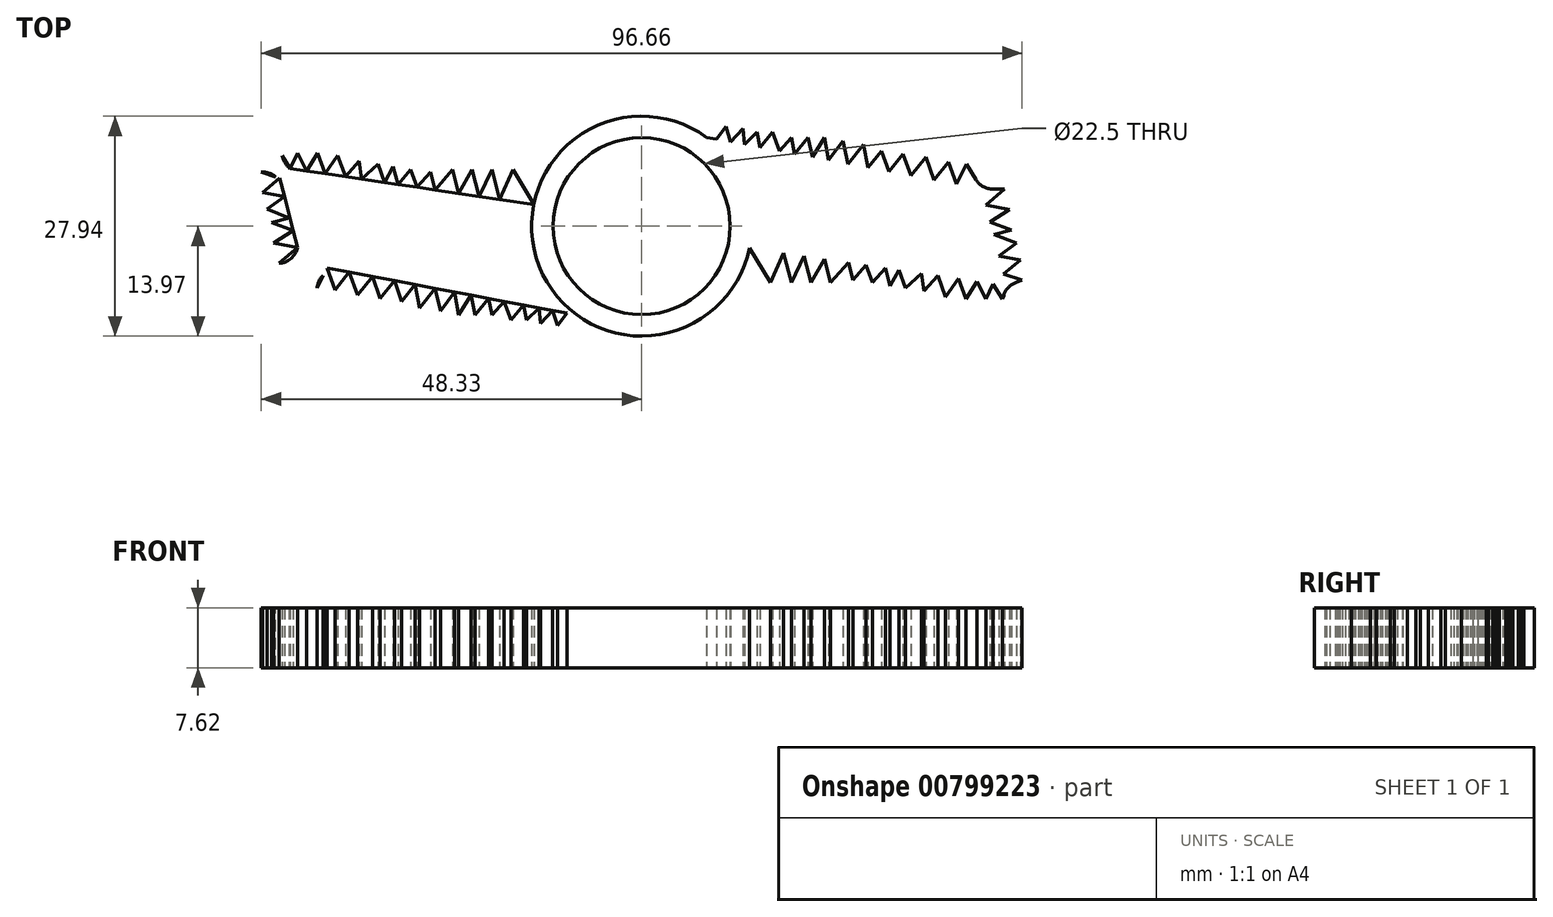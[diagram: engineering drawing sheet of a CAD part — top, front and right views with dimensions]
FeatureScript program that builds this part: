
annotation { "Feature Type Name" : "Feature", "Feature Type Description" : "" }
export const myFeature = defineFeature(function(context is Context, id is Id, definition is map)
    precondition{}
    {
        {
            var Q0;
            Q0=qCreatedBy(makeId("Top.planeOp"),FACE);
            var sketch = newSketch(context, id + "F0", { "sketchPlane" : qUnion([Q0])});
            skCircle(sketch, "E0", {"center": v(0, 0) * mm, "radius": 11.25 * mm});
            skCircle(sketch, "E1", {"center": v(0, 0) * mm, "radius": 13.97 * mm});
            skLineSegment(sketch, "E2", {"start": v(8.24, 11.28) * mm, "end": v(43.2, 4.72) * mm});
            skLineSegment(sketch, "E3", {"start": v(43.2, 4.72) * mm, "end": v(46.36, -7.58) * mm});
            skLineSegment(sketch, "E4", {"start": v(46.36, -7.58) * mm, "end": v(13.7, -2.76) * mm});
            skLineSegment(sketch, "E5.1.0", {"start": v(-43.2, -4.72) * mm, "end": v(-46.36, 7.58) * mm});
            skLineSegment(sketch, "E5.1.1", {"start": v(-8.24, -11.28) * mm, "end": v(-43.2, -4.72) * mm});
            skLineSegment(sketch, "E5.1.2", {"start": v(-46.36, 7.58) * mm, "end": v(-13.7, 2.76) * mm});
            skLineSegment(sketch, "E6", {"start": v(9.5, 11.04) * mm, "end": v(10.7, 12.64) * mm});
            skLineSegment(sketch, "E7", {"start": v(10.7, 12.64) * mm, "end": v(11.3, 10.7) * mm});
            skLineSegment(sketch, "E8", {"start": v(11.3, 10.7) * mm, "end": v(12.87, 12.4) * mm});
            skLineSegment(sketch, "E9", {"start": v(12.87, 12.4) * mm, "end": v(13.06, 10.37) * mm});
            skLineSegment(sketch, "E10", {"start": v(13.06, 10.37) * mm, "end": v(14.64, 11.95) * mm});
            skLineSegment(sketch, "E11", {"start": v(14.64, 11.95) * mm, "end": v(15.02, 10) * mm});
            skLineSegment(sketch, "E12", {"start": v(15.02, 10) * mm, "end": v(16.61, 11.95) * mm});
            skLineSegment(sketch, "E13", {"start": v(16.61, 11.95) * mm, "end": v(17.49, 9.54) * mm});
            skLineSegment(sketch, "E14", {"start": v(17.49, 9.54) * mm, "end": v(19.02, 11.28) * mm});
            skLineSegment(sketch, "E15", {"start": v(19.02, 11.28) * mm, "end": v(19.44, 9.18) * mm});
            skLineSegment(sketch, "E16", {"start": v(19.44, 9.18) * mm, "end": v(21.14, 11.28) * mm});
            skLineSegment(sketch, "E17", {"start": v(21.14, 11.28) * mm, "end": v(21.7, 8.75) * mm});
            skLineSegment(sketch, "E18", {"start": v(21.7, 8.75) * mm, "end": v(23.24, 11.28) * mm});
            skLineSegment(sketch, "E19", {"start": v(23.24, 11.28) * mm, "end": v(23.75, 8.37) * mm});
            skLineSegment(sketch, "E20", {"start": v(23.75, 8.37) * mm, "end": v(25.57, 10.79) * mm});
            skLineSegment(sketch, "E21", {"start": v(25.57, 10.79) * mm, "end": v(26.21, 7.9) * mm});
            skLineSegment(sketch, "E22", {"start": v(26.21, 7.9) * mm, "end": v(28.2, 10.37) * mm});
            skLineSegment(sketch, "E23", {"start": v(28.2, 10.37) * mm, "end": v(28.77, 7.42) * mm});
            skLineSegment(sketch, "E24", {"start": v(28.77, 7.42) * mm, "end": v(30.48, 9.54) * mm});
            skLineSegment(sketch, "E25", {"start": v(30.48, 9.54) * mm, "end": v(31.41, 6.93) * mm});
            skLineSegment(sketch, "E26", {"start": v(31.41, 6.93) * mm, "end": v(33.22, 9.18) * mm});
            skLineSegment(sketch, "E27", {"start": v(33.22, 9.18) * mm, "end": v(34.2, 6.4) * mm});
            skLineSegment(sketch, "E28", {"start": v(34.2, 6.4) * mm, "end": v(36.1, 8.75) * mm});
            skLineSegment(sketch, "E29", {"start": v(36.1, 8.75) * mm, "end": v(37.13, 5.85) * mm});
            skLineSegment(sketch, "E30", {"start": v(37.13, 5.85) * mm, "end": v(38.97, 8.14) * mm});
            skLineSegment(sketch, "E31", {"start": v(38.97, 8.14) * mm, "end": v(39.97, 5.32) * mm});
            skLineSegment(sketch, "E32", {"start": v(39.97, 5.32) * mm, "end": v(41.25, 7.88) * mm});
            skLineSegment(sketch, "E33", {"start": v(41.25, 7.88) * mm, "end": v(43.2, 4.72) * mm});
            skLineSegment(sketch, "E34", {"start": v(43.2, 4.72) * mm, "end": v(46.07, 4.72) * mm});
            skLineSegment(sketch, "E35", {"start": v(46.07, 4.72) * mm, "end": v(43.71, 2.7) * mm});
            skLineSegment(sketch, "E36", {"start": v(43.71, 2.7) * mm, "end": v(46.74, 2.14) * mm});
            skLineSegment(sketch, "E37", {"start": v(46.74, 2.14) * mm, "end": v(44.27, 0.54) * mm});
            skLineSegment(sketch, "E38", {"start": v(44.27, 0.54) * mm, "end": v(47, -0.48) * mm});
            skLineSegment(sketch, "E39", {"start": v(47, -0.48) * mm, "end": v(44.78, -1.06) * mm});
            skPoint(sketch, "E39.endSnap0", {"position": v(44.78, -1.43) * mm});
            skLineSegment(sketch, "E40", {"start": v(44.78, -1.06) * mm, "end": v(47.6, -2.15) * mm});
            skLineSegment(sketch, "E41", {"start": v(47.6, -2.15) * mm, "end": v(45.38, -3.78) * mm});
            skLineSegment(sketch, "E42", {"start": v(45.38, -3.78) * mm, "end": v(48.14, -4.3) * mm});
            skLineSegment(sketch, "E43", {"start": v(48.14, -4.3) * mm, "end": v(45.98, -6.1) * mm});
            skLineSegment(sketch, "E44", {"start": v(45.98, -6.1) * mm, "end": v(48.33, -6.86) * mm});
            skLineSegment(sketch, "E45", {"start": v(48.33, -6.86) * mm, "end": v(46.36, -7.58) * mm});
            skLineSegment(sketch, "E46", {"start": v(46.36, -7.58) * mm, "end": v(45.84, -9.27) * mm});
            skLineSegment(sketch, "E47", {"start": v(45.84, -9.27) * mm, "end": v(44.64, -7.33) * mm});
            skLineSegment(sketch, "E48", {"start": v(44.64, -7.33) * mm, "end": v(43.72, -9.27) * mm});
            skLineSegment(sketch, "E49", {"start": v(43.72, -9.27) * mm, "end": v(42.59, -7.02) * mm});
            skLineSegment(sketch, "E50", {"start": v(42.59, -7.02) * mm, "end": v(41.18, -9.27) * mm});
            skLineSegment(sketch, "E51", {"start": v(41.18, -9.27) * mm, "end": v(40.23, -6.68) * mm});
            skLineSegment(sketch, "E52", {"start": v(40.23, -6.68) * mm, "end": v(38.6, -8.98) * mm});
            skLineSegment(sketch, "E53", {"start": v(38.6, -8.98) * mm, "end": v(37.62, -6.3) * mm});
            skLineSegment(sketch, "E54", {"start": v(37.62, -6.3) * mm, "end": v(35.88, -8.25) * mm});
            skLineSegment(sketch, "E55", {"start": v(35.88, -8.25) * mm, "end": v(35.56, -5.99) * mm});
            skLineSegment(sketch, "E56", {"start": v(35.56, -5.99) * mm, "end": v(33.5, -7.89) * mm});
            skLineSegment(sketch, "E57", {"start": v(33.5, -7.89) * mm, "end": v(32.66, -5.56) * mm});
            skLineSegment(sketch, "E58", {"start": v(32.66, -5.56) * mm, "end": v(31.55, -7.58) * mm});
            skLineSegment(sketch, "E59", {"start": v(31.55, -7.58) * mm, "end": v(30.97, -5.3) * mm});
            skLineSegment(sketch, "E60", {"start": v(30.97, -5.3) * mm, "end": v(29.33, -7.16) * mm});
            skLineSegment(sketch, "E61", {"start": v(29.33, -7.16) * mm, "end": v(28.52, -4.95) * mm});
            skLineSegment(sketch, "E62", {"start": v(28.52, -4.95) * mm, "end": v(26.84, -6.86) * mm});
            skLineSegment(sketch, "E63", {"start": v(26.84, -6.86) * mm, "end": v(26.26, -4.61) * mm});
            skLineSegment(sketch, "E64", {"start": v(26.26, -4.61) * mm, "end": v(24, -7.16) * mm});
            skLineSegment(sketch, "E65", {"start": v(24, -7.16) * mm, "end": v(23.23, -4.17) * mm});
            skLineSegment(sketch, "E66", {"start": v(23.23, -4.17) * mm, "end": v(21.52, -7.16) * mm});
            skLineSegment(sketch, "E67", {"start": v(21.52, -7.16) * mm, "end": v(20.65, -3.78) * mm});
            skLineSegment(sketch, "E68", {"start": v(20.65, -3.78) * mm, "end": v(19.02, -7.16) * mm});
            skLineSegment(sketch, "E69", {"start": v(19.02, -7.16) * mm, "end": v(18.05, -3.4) * mm});
            skLineSegment(sketch, "E70", {"start": v(18.05, -3.4) * mm, "end": v(16.35, -7.16) * mm});
            skLineSegment(sketch, "E71", {"start": v(16.35, -7.16) * mm, "end": v(13.7, -2.76) * mm});
            skPoint(sketch, "E72.1.0", {"position": v(-44.78, 1.43) * mm});
            skLineSegment(sketch, "E72.1.1", {"start": v(-41.18, 9.27) * mm, "end": v(-40.23, 6.68) * mm});
            skLineSegment(sketch, "E72.1.2", {"start": v(-38.6, 8.98) * mm, "end": v(-37.62, 6.3) * mm});
            skLineSegment(sketch, "E72.1.3", {"start": v(-39.97, -5.32) * mm, "end": v(-41.25, -7.88) * mm});
            skLineSegment(sketch, "E72.1.4", {"start": v(-35.88, 8.25) * mm, "end": v(-35.56, 5.99) * mm});
            skLineSegment(sketch, "E72.1.5", {"start": v(-28.2, -10.37) * mm, "end": v(-28.77, -7.42) * mm});
            skLineSegment(sketch, "E72.1.6", {"start": v(-43.71, -2.7) * mm, "end": v(-46.74, -2.14) * mm});
            skLineSegment(sketch, "E72.1.7", {"start": v(-30.48, -9.54) * mm, "end": v(-31.41, -6.93) * mm});
            skLineSegment(sketch, "E72.1.9", {"start": v(-44.64, 7.33) * mm, "end": v(-43.72, 9.27) * mm});
            skLineSegment(sketch, "E72.1.10", {"start": v(-34.2, -6.4) * mm, "end": v(-36.1, -8.75) * mm});
            skLineSegment(sketch, "E72.1.11", {"start": v(-19.44, -9.18) * mm, "end": v(-21.14, -11.28) * mm});
            skLineSegment(sketch, "E72.1.12", {"start": v(-10.7, -12.64) * mm, "end": v(-11.3, -10.7) * mm});
            skLineSegment(sketch, "E72.1.13", {"start": v(-16.35, 7.16) * mm, "end": v(-13.7, 2.76) * mm});
            skLineSegment(sketch, "E72.1.14", {"start": v(-28.77, -7.42) * mm, "end": v(-30.48, -9.54) * mm});
            skLineSegment(sketch, "E72.1.15", {"start": v(-16.61, -11.95) * mm, "end": v(-17.49, -9.54) * mm});
            skLineSegment(sketch, "E72.1.16", {"start": v(-13.06, -10.37) * mm, "end": v(-14.64, -11.95) * mm});
            skLineSegment(sketch, "E72.1.17", {"start": v(-23.75, -8.37) * mm, "end": v(-25.57, -10.79) * mm});
            skLineSegment(sketch, "E72.1.18", {"start": v(-31.41, -6.93) * mm, "end": v(-33.22, -9.18) * mm});
            skLineSegment(sketch, "E72.1.19", {"start": v(-33.22, -9.18) * mm, "end": v(-34.2, -6.4) * mm});
            skLineSegment(sketch, "E72.1.20", {"start": v(-23.24, -11.28) * mm, "end": v(-23.75, -8.37) * mm});
            skLineSegment(sketch, "E72.1.21", {"start": v(-23.23, 4.17) * mm, "end": v(-21.52, 7.16) * mm});
            skLineSegment(sketch, "E72.1.22", {"start": v(-19.02, -11.28) * mm, "end": v(-19.44, -9.18) * mm});
            skLineSegment(sketch, "E72.1.23", {"start": v(-25.57, -10.79) * mm, "end": v(-26.21, -7.9) * mm});
            skLineSegment(sketch, "E72.1.24", {"start": v(-46.74, -2.14) * mm, "end": v(-44.27, -0.54) * mm});
            skLineSegment(sketch, "E72.1.25", {"start": v(-26.84, 6.86) * mm, "end": v(-26.26, 4.61) * mm});
            skLineSegment(sketch, "E72.1.26", {"start": v(-43.72, 9.27) * mm, "end": v(-42.59, 7.02) * mm});
            skLineSegment(sketch, "E72.1.27", {"start": v(-38.97, -8.14) * mm, "end": v(-39.97, -5.32) * mm});
            skLineSegment(sketch, "E72.1.28", {"start": v(-40.23, 6.68) * mm, "end": v(-38.6, 8.98) * mm});
            skLineSegment(sketch, "E72.1.29", {"start": v(-21.14, -11.28) * mm, "end": v(-21.7, -8.75) * mm});
            skLineSegment(sketch, "E72.1.30", {"start": v(-21.7, -8.75) * mm, "end": v(-23.24, -11.28) * mm});
            skLineSegment(sketch, "E72.1.31", {"start": v(-35.56, 5.99) * mm, "end": v(-33.5, 7.89) * mm});
            skLineSegment(sketch, "E72.1.32", {"start": v(-26.26, 4.61) * mm, "end": v(-24, 7.16) * mm});
            skLineSegment(sketch, "E72.1.33", {"start": v(-24, 7.16) * mm, "end": v(-23.23, 4.17) * mm});
            skLineSegment(sketch, "E72.1.34", {"start": v(-15.02, -10) * mm, "end": v(-16.61, -11.95) * mm});
            skLineSegment(sketch, "E72.1.35", {"start": v(-36.1, -8.75) * mm, "end": v(-37.13, -5.85) * mm});
            skLineSegment(sketch, "E72.1.36", {"start": v(-42.59, 7.02) * mm, "end": v(-41.18, 9.27) * mm});
            skLineSegment(sketch, "E72.1.38", {"start": v(-21.52, 7.16) * mm, "end": v(-20.65, 3.78) * mm});
            skLineSegment(sketch, "E72.1.39", {"start": v(-11.3, -10.7) * mm, "end": v(-12.87, -12.4) * mm});
            skLineSegment(sketch, "E72.1.40", {"start": v(-37.62, 6.3) * mm, "end": v(-35.88, 8.25) * mm});
            skLineSegment(sketch, "E72.1.41", {"start": v(-37.13, -5.85) * mm, "end": v(-38.97, -8.14) * mm});
            skLineSegment(sketch, "E72.1.42", {"start": v(-26.21, -7.9) * mm, "end": v(-28.2, -10.37) * mm});
            skLineSegment(sketch, "E72.1.43", {"start": v(-28.52, 4.95) * mm, "end": v(-26.84, 6.86) * mm});
            skLineSegment(sketch, "E72.1.44", {"start": v(-12.87, -12.4) * mm, "end": v(-13.06, -10.37) * mm});
            skLineSegment(sketch, "E72.1.45", {"start": v(-29.33, 7.16) * mm, "end": v(-28.52, 4.95) * mm});
            skLineSegment(sketch, "E72.1.46", {"start": v(-41.25, -7.88) * mm, "end": v(-43.2, -4.72) * mm});
            skLineSegment(sketch, "E72.1.47", {"start": v(-46.07, -4.72) * mm, "end": v(-43.71, -2.7) * mm});
            skLineSegment(sketch, "E72.1.48", {"start": v(-20.65, 3.78) * mm, "end": v(-19.02, 7.16) * mm});
            skLineSegment(sketch, "E72.1.49", {"start": v(-9.5, -11.04) * mm, "end": v(-10.7, -12.64) * mm});
            skLineSegment(sketch, "E72.1.50", {"start": v(-44.78, 1.06) * mm, "end": v(-47.6, 2.15) * mm});
            skLineSegment(sketch, "E72.1.51", {"start": v(-14.64, -11.95) * mm, "end": v(-15.02, -10) * mm});
            skLineSegment(sketch, "E72.1.52", {"start": v(-43.2, -4.72) * mm, "end": v(-46.07, -4.72) * mm});
            skLineSegment(sketch, "E72.1.53", {"start": v(-18.05, 3.4) * mm, "end": v(-16.35, 7.16) * mm});
            skLineSegment(sketch, "E72.1.54", {"start": v(-17.49, -9.54) * mm, "end": v(-19.02, -11.28) * mm});
            skLineSegment(sketch, "E72.1.55", {"start": v(-44.27, -0.54) * mm, "end": v(-47, 0.48) * mm});
            skLineSegment(sketch, "E72.1.56", {"start": v(-31.55, 7.58) * mm, "end": v(-30.97, 5.3) * mm});
            skLineSegment(sketch, "E72.1.57", {"start": v(-32.66, 5.56) * mm, "end": v(-31.55, 7.58) * mm});
            skLineSegment(sketch, "E72.1.59", {"start": v(-47, 0.48) * mm, "end": v(-44.78, 1.06) * mm});
            skLineSegment(sketch, "E72.1.60", {"start": v(-33.5, 7.89) * mm, "end": v(-32.66, 5.56) * mm});
            skLineSegment(sketch, "E72.1.61", {"start": v(-30.97, 5.3) * mm, "end": v(-29.33, 7.16) * mm});
            skLineSegment(sketch, "E72.1.62", {"start": v(-47.6, 2.15) * mm, "end": v(-45.38, 3.78) * mm});
            skLineSegment(sketch, "E72.1.63", {"start": v(-19.02, 7.16) * mm, "end": v(-18.05, 3.4) * mm});
            skLineSegment(sketch, "E72.1.64", {"start": v(-48.33, 6.86) * mm, "end": v(-46.36, 7.58) * mm});
            skLineSegment(sketch, "E72.1.65", {"start": v(-45.84, 9.27) * mm, "end": v(-44.64, 7.33) * mm});
            skLineSegment(sketch, "E72.1.66", {"start": v(-45.98, 6.1) * mm, "end": v(-48.33, 6.86) * mm});
            skLineSegment(sketch, "E72.1.67", {"start": v(-46.36, 7.58) * mm, "end": v(-45.84, 9.27) * mm});
            skLineSegment(sketch, "E72.1.68", {"start": v(-45.38, 3.78) * mm, "end": v(-48.14, 4.3) * mm});
            skLineSegment(sketch, "E72.1.69", {"start": v(-48.14, 4.3) * mm, "end": v(-45.98, 6.1) * mm});
            skSolve(sketch);
        }
        {
            var Q0;
            Q0=makeQuery(id+"F0.imprint","IMPRINT",FACE,{"disambiguationData":[TD([[makeQuery(id+"F0.imprint","IMPRINT",EDGE,{"derivedFrom":sQuery(id+"F0.wireOp",EDGE,"E0")}),-1.0]])]});
            var Q1;
            {var subQ8=sQuery(id+"F0.wireOp",EDGE,"E2");var subQ19=sQuery(id+"F0.wireOp",EDGE,"E1");var subQ20=makeQuery(id+"F0.imprint","INTERSECT",VERTEX,{"derivedFrom":[subQ19,subQ8]});Q1=makeQuery(id+"F0.imprint","IMPRINT",FACE,{"disambiguationData":[TD([[makeQuery(id+"F0.imprint","IMPRINT",EDGE,{"disambiguationData":[TD([[subQ20,-1.0]])],"derivedFrom":subQ8}),-1.0]])]});}
            var Q2;
            {var subQ6=sQuery(id+"F0.wireOp",EDGE,"E5.1.1");var subQ21=sQuery(id+"F0.wireOp",EDGE,"E1");var subQ22=makeQuery(id+"F0.imprint","INTERSECT",VERTEX,{"derivedFrom":[subQ21,subQ6]});Q2=makeQuery(id+"F0.imprint","IMPRINT",FACE,{"disambiguationData":[TD([[makeQuery(id+"F0.imprint","IMPRINT",EDGE,{"disambiguationData":[TD([[subQ22,-1.0]])],"derivedFrom":subQ6}),-1.0]])]});}
            var Q3;
            {var subQ0=sQuery(id+"F0.wireOp",EDGE,"E6");Q3=makeQuery(id+"F0.imprint","IMPRINT",FACE,{"disambiguationData":[TD([[makeQuery(id+"F0.imprint","IMPRINT",EDGE,{"derivedFrom":subQ0}),-1.0]])]});}
            var Q4;
            {var subQ0=sQuery(id+"F0.wireOp",EDGE,"E8");Q4=makeQuery(id+"F0.imprint","IMPRINT",FACE,{"disambiguationData":[TD([[makeQuery(id+"F0.imprint","IMPRINT",EDGE,{"derivedFrom":subQ0}),-1.0]])]});}
            var Q5;
            {var subQ0=sQuery(id+"F0.wireOp",EDGE,"E10");Q5=makeQuery(id+"F0.imprint","IMPRINT",FACE,{"disambiguationData":[TD([[makeQuery(id+"F0.imprint","IMPRINT",EDGE,{"derivedFrom":subQ0}),-1.0]])]});}
            var Q6;
            {var subQ0=sQuery(id+"F0.wireOp",EDGE,"E12");Q6=makeQuery(id+"F0.imprint","IMPRINT",FACE,{"disambiguationData":[TD([[makeQuery(id+"F0.imprint","IMPRINT",EDGE,{"derivedFrom":subQ0}),-1.0]])]});}
            var Q7;
            {var subQ0=sQuery(id+"F0.wireOp",EDGE,"E14");Q7=makeQuery(id+"F0.imprint","IMPRINT",FACE,{"disambiguationData":[TD([[makeQuery(id+"F0.imprint","IMPRINT",EDGE,{"derivedFrom":subQ0}),-1.0]])]});}
            var Q8;
            {var subQ0=sQuery(id+"F0.wireOp",EDGE,"E16");Q8=makeQuery(id+"F0.imprint","IMPRINT",FACE,{"disambiguationData":[TD([[makeQuery(id+"F0.imprint","IMPRINT",EDGE,{"derivedFrom":subQ0}),-1.0]])]});}
            var Q9;
            {var subQ0=sQuery(id+"F0.wireOp",EDGE,"E18");Q9=makeQuery(id+"F0.imprint","IMPRINT",FACE,{"disambiguationData":[TD([[makeQuery(id+"F0.imprint","IMPRINT",EDGE,{"derivedFrom":subQ0}),-1.0]])]});}
            var Q10;
            {var subQ0=sQuery(id+"F0.wireOp",EDGE,"E20");Q10=makeQuery(id+"F0.imprint","IMPRINT",FACE,{"disambiguationData":[TD([[makeQuery(id+"F0.imprint","IMPRINT",EDGE,{"derivedFrom":subQ0}),-1.0]])]});}
            var Q11;
            {var subQ0=sQuery(id+"F0.wireOp",EDGE,"E22");Q11=makeQuery(id+"F0.imprint","IMPRINT",FACE,{"disambiguationData":[TD([[makeQuery(id+"F0.imprint","IMPRINT",EDGE,{"derivedFrom":subQ0}),-1.0]])]});}
            var Q12;
            {var subQ0=sQuery(id+"F0.wireOp",EDGE,"E24");Q12=makeQuery(id+"F0.imprint","IMPRINT",FACE,{"disambiguationData":[TD([[makeQuery(id+"F0.imprint","IMPRINT",EDGE,{"derivedFrom":subQ0}),-1.0]])]});}
            var Q13;
            {var subQ0=sQuery(id+"F0.wireOp",EDGE,"E26");Q13=makeQuery(id+"F0.imprint","IMPRINT",FACE,{"disambiguationData":[TD([[makeQuery(id+"F0.imprint","IMPRINT",EDGE,{"derivedFrom":subQ0}),-1.0]])]});}
            var Q14;
            {var subQ0=sQuery(id+"F0.wireOp",EDGE,"E28");Q14=makeQuery(id+"F0.imprint","IMPRINT",FACE,{"disambiguationData":[TD([[makeQuery(id+"F0.imprint","IMPRINT",EDGE,{"derivedFrom":subQ0}),-1.0]])]});}
            var Q15;
            {var subQ0=sQuery(id+"F0.wireOp",EDGE,"E30");Q15=makeQuery(id+"F0.imprint","IMPRINT",FACE,{"disambiguationData":[TD([[makeQuery(id+"F0.imprint","IMPRINT",EDGE,{"derivedFrom":subQ0}),-1.0]])]});}
            var Q16;
            {var subQ2=sQuery(id+"F0.wireOp",EDGE,"E32");Q16=makeQuery(id+"F0.imprint","IMPRINT",FACE,{"disambiguationData":[TD([[makeQuery(id+"F0.imprint","IMPRINT",EDGE,{"derivedFrom":subQ2}),-1.0]])]});}
            var Q17;
            {var subQ0=sQuery(id+"F0.wireOp",EDGE,"E34");Q17=makeQuery(id+"F0.imprint","IMPRINT",FACE,{"disambiguationData":[TD([[makeQuery(id+"F0.imprint","IMPRINT",EDGE,{"derivedFrom":subQ0}),-1.0]])]});}
            var Q18;
            {var subQ0=sQuery(id+"F0.wireOp",EDGE,"E36");Q18=makeQuery(id+"F0.imprint","IMPRINT",FACE,{"disambiguationData":[TD([[makeQuery(id+"F0.imprint","IMPRINT",EDGE,{"derivedFrom":subQ0}),-1.0]])]});}
            var Q19;
            {var subQ0=sQuery(id+"F0.wireOp",EDGE,"E38");Q19=makeQuery(id+"F0.imprint","IMPRINT",FACE,{"disambiguationData":[TD([[makeQuery(id+"F0.imprint","IMPRINT",EDGE,{"derivedFrom":subQ0}),-1.0]])]});}
            var Q20;
            {var subQ0=sQuery(id+"F0.wireOp",EDGE,"E42");Q20=makeQuery(id+"F0.imprint","IMPRINT",FACE,{"disambiguationData":[TD([[makeQuery(id+"F0.imprint","IMPRINT",EDGE,{"derivedFrom":subQ0}),-1.0]])]});}
            var Q21;
            {var subQ2=sQuery(id+"F0.wireOp",EDGE,"E44");Q21=makeQuery(id+"F0.imprint","IMPRINT",FACE,{"disambiguationData":[TD([[makeQuery(id+"F0.imprint","IMPRINT",EDGE,{"derivedFrom":subQ2}),-1.0]])]});}
            var Q22;
            {var subQ0=sQuery(id+"F0.wireOp",EDGE,"E46");Q22=makeQuery(id+"F0.imprint","IMPRINT",FACE,{"disambiguationData":[TD([[makeQuery(id+"F0.imprint","IMPRINT",EDGE,{"derivedFrom":subQ0}),-1.0]])]});}
            var Q23;
            {var subQ0=sQuery(id+"F0.wireOp",EDGE,"E48");Q23=makeQuery(id+"F0.imprint","IMPRINT",FACE,{"disambiguationData":[TD([[makeQuery(id+"F0.imprint","IMPRINT",EDGE,{"derivedFrom":subQ0}),-1.0]])]});}
            var Q24;
            {var subQ0=sQuery(id+"F0.wireOp",EDGE,"E50");Q24=makeQuery(id+"F0.imprint","IMPRINT",FACE,{"disambiguationData":[TD([[makeQuery(id+"F0.imprint","IMPRINT",EDGE,{"derivedFrom":subQ0}),-1.0]])]});}
            var Q25;
            {var subQ0=sQuery(id+"F0.wireOp",EDGE,"E52");Q25=makeQuery(id+"F0.imprint","IMPRINT",FACE,{"disambiguationData":[TD([[makeQuery(id+"F0.imprint","IMPRINT",EDGE,{"derivedFrom":subQ0}),-1.0]])]});}
            var Q26;
            {var subQ0=sQuery(id+"F0.wireOp",EDGE,"E54");Q26=makeQuery(id+"F0.imprint","IMPRINT",FACE,{"disambiguationData":[TD([[makeQuery(id+"F0.imprint","IMPRINT",EDGE,{"derivedFrom":subQ0}),-1.0]])]});}
            var Q27;
            {var subQ0=sQuery(id+"F0.wireOp",EDGE,"E56");Q27=makeQuery(id+"F0.imprint","IMPRINT",FACE,{"disambiguationData":[TD([[makeQuery(id+"F0.imprint","IMPRINT",EDGE,{"derivedFrom":subQ0}),-1.0]])]});}
            var Q28;
            {var subQ0=sQuery(id+"F0.wireOp",EDGE,"E58");Q28=makeQuery(id+"F0.imprint","IMPRINT",FACE,{"disambiguationData":[TD([[makeQuery(id+"F0.imprint","IMPRINT",EDGE,{"derivedFrom":subQ0}),-1.0]])]});}
            var Q29;
            {var subQ0=sQuery(id+"F0.wireOp",EDGE,"E60");Q29=makeQuery(id+"F0.imprint","IMPRINT",FACE,{"disambiguationData":[TD([[makeQuery(id+"F0.imprint","IMPRINT",EDGE,{"derivedFrom":subQ0}),-1.0]])]});}
            var Q30;
            {var subQ0=sQuery(id+"F0.wireOp",EDGE,"E62");Q30=makeQuery(id+"F0.imprint","IMPRINT",FACE,{"disambiguationData":[TD([[makeQuery(id+"F0.imprint","IMPRINT",EDGE,{"derivedFrom":subQ0}),-1.0]])]});}
            var Q31;
            {var subQ0=sQuery(id+"F0.wireOp",EDGE,"E64");Q31=makeQuery(id+"F0.imprint","IMPRINT",FACE,{"disambiguationData":[TD([[makeQuery(id+"F0.imprint","IMPRINT",EDGE,{"derivedFrom":subQ0}),-1.0]])]});}
            var Q32;
            {var subQ0=sQuery(id+"F0.wireOp",EDGE,"E66");Q32=makeQuery(id+"F0.imprint","IMPRINT",FACE,{"disambiguationData":[TD([[makeQuery(id+"F0.imprint","IMPRINT",EDGE,{"derivedFrom":subQ0}),-1.0]])]});}
            var Q33;
            {var subQ0=sQuery(id+"F0.wireOp",EDGE,"E68");Q33=makeQuery(id+"F0.imprint","IMPRINT",FACE,{"disambiguationData":[TD([[makeQuery(id+"F0.imprint","IMPRINT",EDGE,{"derivedFrom":subQ0}),-1.0]])]});}
            var Q34;
            {var subQ2=sQuery(id+"F0.wireOp",EDGE,"E70");Q34=makeQuery(id+"F0.imprint","IMPRINT",FACE,{"disambiguationData":[TD([[makeQuery(id+"F0.imprint","IMPRINT",EDGE,{"derivedFrom":subQ2}),-1.0]])]});}
            var Q35;
            {var subQ0=sQuery(id+"F0.wireOp",EDGE,"E72.1.12");Q35=makeQuery(id+"F0.imprint","IMPRINT",FACE,{"disambiguationData":[TD([[makeQuery(id+"F0.imprint","IMPRINT",EDGE,{"derivedFrom":subQ0}),-1.0]])]});}
            var Q36;
            {var subQ0=sQuery(id+"F0.wireOp",EDGE,"E72.1.39");Q36=makeQuery(id+"F0.imprint","IMPRINT",FACE,{"disambiguationData":[TD([[makeQuery(id+"F0.imprint","IMPRINT",EDGE,{"derivedFrom":subQ0}),-1.0]])]});}
            var Q37;
            {var subQ0=sQuery(id+"F0.wireOp",EDGE,"E72.1.16");Q37=makeQuery(id+"F0.imprint","IMPRINT",FACE,{"disambiguationData":[TD([[makeQuery(id+"F0.imprint","IMPRINT",EDGE,{"derivedFrom":subQ0}),-1.0]])]});}
            var Q38;
            {var subQ0=sQuery(id+"F0.wireOp",EDGE,"E72.1.15");Q38=makeQuery(id+"F0.imprint","IMPRINT",FACE,{"disambiguationData":[TD([[makeQuery(id+"F0.imprint","IMPRINT",EDGE,{"derivedFrom":subQ0}),-1.0]])]});}
            var Q39;
            {var subQ0=sQuery(id+"F0.wireOp",EDGE,"E72.1.22");Q39=makeQuery(id+"F0.imprint","IMPRINT",FACE,{"disambiguationData":[TD([[makeQuery(id+"F0.imprint","IMPRINT",EDGE,{"derivedFrom":subQ0}),-1.0]])]});}
            var Q40;
            {var subQ0=sQuery(id+"F0.wireOp",EDGE,"E72.1.11");Q40=makeQuery(id+"F0.imprint","IMPRINT",FACE,{"disambiguationData":[TD([[makeQuery(id+"F0.imprint","IMPRINT",EDGE,{"derivedFrom":subQ0}),-1.0]])]});}
            var Q41;
            {var subQ0=sQuery(id+"F0.wireOp",EDGE,"E72.1.20");Q41=makeQuery(id+"F0.imprint","IMPRINT",FACE,{"disambiguationData":[TD([[makeQuery(id+"F0.imprint","IMPRINT",EDGE,{"derivedFrom":subQ0}),-1.0]])]});}
            var Q42;
            {var subQ0=sQuery(id+"F0.wireOp",EDGE,"E72.1.17");Q42=makeQuery(id+"F0.imprint","IMPRINT",FACE,{"disambiguationData":[TD([[makeQuery(id+"F0.imprint","IMPRINT",EDGE,{"derivedFrom":subQ0}),-1.0]])]});}
            var Q43;
            {var subQ0=sQuery(id+"F0.wireOp",EDGE,"E72.1.5");Q43=makeQuery(id+"F0.imprint","IMPRINT",FACE,{"disambiguationData":[TD([[makeQuery(id+"F0.imprint","IMPRINT",EDGE,{"derivedFrom":subQ0}),-1.0]])]});}
            var Q44;
            {var subQ0=sQuery(id+"F0.wireOp",EDGE,"E72.1.18");Q44=makeQuery(id+"F0.imprint","IMPRINT",FACE,{"disambiguationData":[TD([[makeQuery(id+"F0.imprint","IMPRINT",EDGE,{"derivedFrom":subQ0}),-1.0]])]});}
            var Q45;
            {var subQ0=sQuery(id+"F0.wireOp",EDGE,"E72.1.27");Q45=makeQuery(id+"F0.imprint","IMPRINT",FACE,{"disambiguationData":[TD([[makeQuery(id+"F0.imprint","IMPRINT",EDGE,{"derivedFrom":subQ0}),-1.0]])]});}
            var Q46;
            {var subQ0=sQuery(id+"F0.wireOp",EDGE,"E72.1.3");Q46=makeQuery(id+"F0.imprint","IMPRINT",FACE,{"disambiguationData":[TD([[makeQuery(id+"F0.imprint","IMPRINT",EDGE,{"derivedFrom":subQ0}),-1.0]])]});}
            var Q47;
            {var subQ0=sQuery(id+"F0.wireOp",EDGE,"E72.1.7");Q47=makeQuery(id+"F0.imprint","IMPRINT",FACE,{"disambiguationData":[TD([[makeQuery(id+"F0.imprint","IMPRINT",EDGE,{"derivedFrom":subQ0}),-1.0]])]});}
            var Q48;
            {var subQ0=sQuery(id+"F0.wireOp",EDGE,"E72.1.10");Q48=makeQuery(id+"F0.imprint","IMPRINT",FACE,{"disambiguationData":[TD([[makeQuery(id+"F0.imprint","IMPRINT",EDGE,{"derivedFrom":subQ0}),-1.0]])]});}
            var Q49;
            {var subQ0=sQuery(id+"F0.wireOp",EDGE,"E72.1.47");Q49=makeQuery(id+"F0.imprint","IMPRINT",FACE,{"disambiguationData":[TD([[makeQuery(id+"F0.imprint","IMPRINT",EDGE,{"derivedFrom":subQ0}),-1.0]])]});}
            var Q50;
            {var subQ0=sQuery(id+"F0.wireOp",EDGE,"E72.1.6");Q50=makeQuery(id+"F0.imprint","IMPRINT",FACE,{"disambiguationData":[TD([[makeQuery(id+"F0.imprint","IMPRINT",EDGE,{"derivedFrom":subQ0}),-1.0]])]});}
            var Q51;
            {var subQ0=sQuery(id+"F0.wireOp",EDGE,"E72.1.68");Q51=makeQuery(id+"F0.imprint","IMPRINT",FACE,{"disambiguationData":[TD([[makeQuery(id+"F0.imprint","IMPRINT",EDGE,{"derivedFrom":subQ0}),-1.0]])]});}
            var Q52;
            {var subQ0=sQuery(id+"F0.wireOp",EDGE,"E72.1.64");Q52=makeQuery(id+"F0.imprint","IMPRINT",FACE,{"disambiguationData":[TD([[makeQuery(id+"F0.imprint","IMPRINT",EDGE,{"derivedFrom":subQ0}),-1.0]])]});}
            var Q53;
            {var subQ0=sQuery(id+"F0.wireOp",EDGE,"E72.1.65");Q53=makeQuery(id+"F0.imprint","IMPRINT",FACE,{"disambiguationData":[TD([[makeQuery(id+"F0.imprint","IMPRINT",EDGE,{"derivedFrom":subQ0}),-1.0]])]});}
            var Q54;
            {var subQ0=sQuery(id+"F0.wireOp",EDGE,"E72.1.9");Q54=makeQuery(id+"F0.imprint","IMPRINT",FACE,{"disambiguationData":[TD([[makeQuery(id+"F0.imprint","IMPRINT",EDGE,{"derivedFrom":subQ0}),-1.0]])]});}
            var Q55;
            {var subQ0=sQuery(id+"F0.wireOp",EDGE,"E72.1.1");Q55=makeQuery(id+"F0.imprint","IMPRINT",FACE,{"disambiguationData":[TD([[makeQuery(id+"F0.imprint","IMPRINT",EDGE,{"derivedFrom":subQ0}),-1.0]])]});}
            var Q56;
            {var subQ0=sQuery(id+"F0.wireOp",EDGE,"E72.1.2");Q56=makeQuery(id+"F0.imprint","IMPRINT",FACE,{"disambiguationData":[TD([[makeQuery(id+"F0.imprint","IMPRINT",EDGE,{"derivedFrom":subQ0}),-1.0]])]});}
            var Q57;
            {var subQ0=sQuery(id+"F0.wireOp",EDGE,"E72.1.4");Q57=makeQuery(id+"F0.imprint","IMPRINT",FACE,{"disambiguationData":[TD([[makeQuery(id+"F0.imprint","IMPRINT",EDGE,{"derivedFrom":subQ0}),-1.0]])]});}
            var Q58;
            {var subQ0=sQuery(id+"F0.wireOp",EDGE,"E72.1.56");Q58=makeQuery(id+"F0.imprint","IMPRINT",FACE,{"disambiguationData":[TD([[makeQuery(id+"F0.imprint","IMPRINT",EDGE,{"derivedFrom":subQ0}),-1.0]])]});}
            var Q59;
            {var subQ0=sQuery(id+"F0.wireOp",EDGE,"E72.1.45");Q59=makeQuery(id+"F0.imprint","IMPRINT",FACE,{"disambiguationData":[TD([[makeQuery(id+"F0.imprint","IMPRINT",EDGE,{"derivedFrom":subQ0}),-1.0]])]});}
            var Q60;
            {var subQ0=sQuery(id+"F0.wireOp",EDGE,"E72.1.25");Q60=makeQuery(id+"F0.imprint","IMPRINT",FACE,{"disambiguationData":[TD([[makeQuery(id+"F0.imprint","IMPRINT",EDGE,{"derivedFrom":subQ0}),-1.0]])]});}
            var Q61;
            Q61=makeQuery(id+"F0.imprint","IMPRINT",FACE,{"disambiguationData":[TD([[makeQuery(id+"F0.imprint","IMPRINT",EDGE,{"derivedFrom":sQuery(id+"F0.wireOp",EDGE,"E72.1.50")}),-1.0]])]});
            var Q62;
            {var subQ0=sQuery(id+"F0.wireOp",EDGE,"E72.1.31");Q62=makeQuery(id+"F0.imprint","IMPRINT",FACE,{"disambiguationData":[TD([[makeQuery(id+"F0.imprint","IMPRINT",EDGE,{"derivedFrom":subQ0}),-1.0]])]});}
            var Q63;
            {var subQ0=sQuery(id+"F0.wireOp",EDGE,"E72.1.32");Q63=makeQuery(id+"F0.imprint","IMPRINT",FACE,{"disambiguationData":[TD([[makeQuery(id+"F0.imprint","IMPRINT",EDGE,{"derivedFrom":subQ0}),-1.0]])]});}
            var Q64;
            {var subQ0=sQuery(id+"F0.wireOp",EDGE,"E72.1.21");Q64=makeQuery(id+"F0.imprint","IMPRINT",FACE,{"disambiguationData":[TD([[makeQuery(id+"F0.imprint","IMPRINT",EDGE,{"derivedFrom":subQ0}),-1.0]])]});}
            var Q65;
            {var subQ0=sQuery(id+"F0.wireOp",EDGE,"E72.1.48");Q65=makeQuery(id+"F0.imprint","IMPRINT",FACE,{"disambiguationData":[TD([[makeQuery(id+"F0.imprint","IMPRINT",EDGE,{"derivedFrom":subQ0}),-1.0]])]});}
            var Q66;
            {var subQ0=sQuery(id+"F0.wireOp",EDGE,"E72.1.13");Q66=makeQuery(id+"F0.imprint","IMPRINT",FACE,{"disambiguationData":[TD([[makeQuery(id+"F0.imprint","IMPRINT",EDGE,{"derivedFrom":subQ0}),-1.0]])]});}
            extrude(context, id + "F1", {"entities" : qUnion([Q0, Q1, Q2, Q3, Q4, Q5, Q6, Q7, Q8, Q9, Q10, Q11, Q12, Q13, Q14, Q15, Q16, Q17, Q18, Q19, Q20, Q21, Q22, Q23, Q24, Q25, Q26, Q27, Q28, Q29, Q30, Q31, Q32, Q33, Q34, Q35, Q36, Q37, Q38, Q39, Q40, Q41, Q42, Q43, Q44, Q45, Q46, Q47, Q48, Q49, Q50, Q51, Q52, Q53, Q54, Q55, Q56, Q57, Q58, Q59, Q60, Q61, Q62, Q63, Q64, Q65, Q66]), "depth" : 7.62 * mm, "offsetDistance" : 25.4 * mm});
        }
        {
            var Q0;
            Q0=makeQuery(id+"F1.opExtrude","SWEPT_EDGE",EDGE,{"disambiguationData":[OSD([sQuery(id+"F0.wireOp",EDGE,"E5.1.2"),sQuery(id+"F0.wireOp",EDGE,"E5.1.0"),sQuery(id+"F0.wireOp",EDGE,"E72.1.64"),sQuery(id+"F0.wireOp",EDGE,"E72.1.67")])]});
            var Q1;
            Q1=makeQuery(id+"F1.opExtrude","SWEPT_EDGE",EDGE,{"disambiguationData":[OSD([sQuery(id+"F0.wireOp",EDGE,"E5.1.1"),sQuery(id+"F0.wireOp",EDGE,"E72.1.46"),sQuery(id+"F0.wireOp",EDGE,"E72.1.52"),sQuery(id+"F0.wireOp",EDGE,"E5.1.0")])]});
            var Q2;
            Q2=makeQuery(id+"F1.opExtrude","SWEPT_EDGE",EDGE,{"disambiguationData":[OSD([sQuery(id+"F0.wireOp",EDGE,"E3"),sQuery(id+"F0.wireOp",EDGE,"E4"),sQuery(id+"F0.wireOp",EDGE,"E45"),sQuery(id+"F0.wireOp",EDGE,"E46")])]});
            var Q3;
            Q3=makeQuery(id+"F1.opExtrude","SWEPT_EDGE",EDGE,{"disambiguationData":[OSD([sQuery(id+"F0.wireOp",EDGE,"E2"),sQuery(id+"F0.wireOp",EDGE,"E3"),sQuery(id+"F0.wireOp",EDGE,"E33"),sQuery(id+"F0.wireOp",EDGE,"E34")])]});
            fillet(context, id + "F2", {"entities" : qUnion([Q0, Q1, Q2, Q3]), "radius" : 2.54 * mm, "tangentPropagation" : true, "allowEdgeOverflow" : false});
        }
    });
